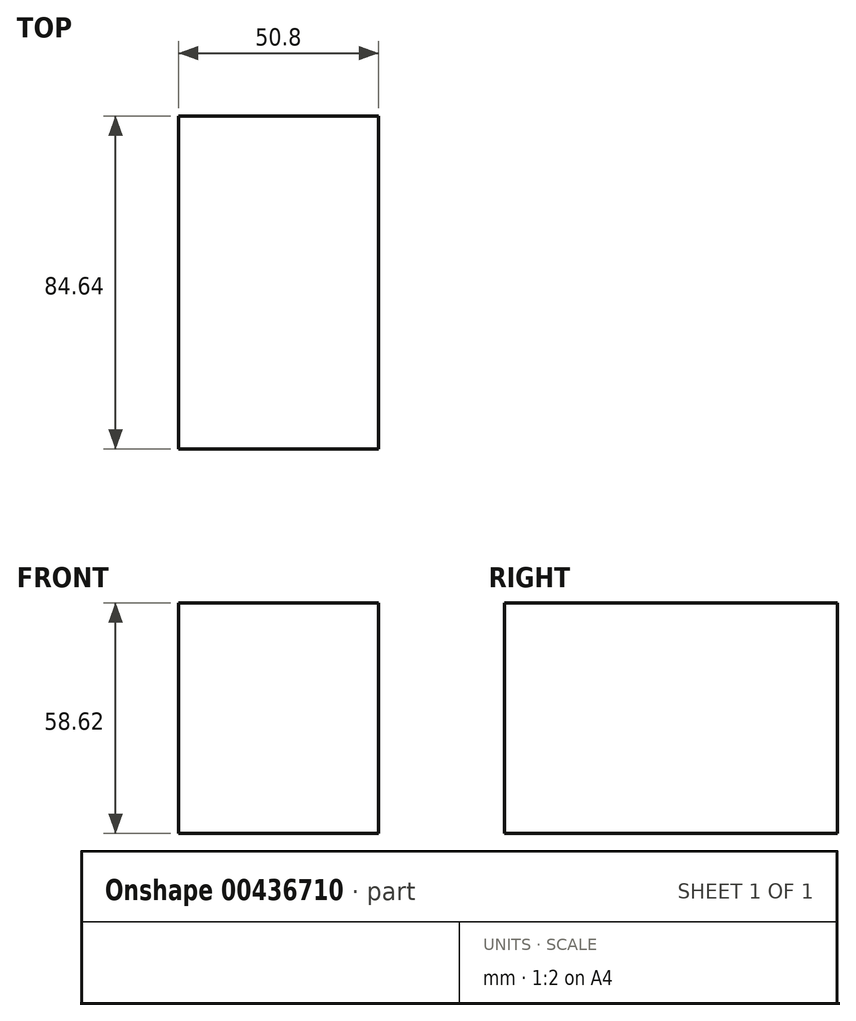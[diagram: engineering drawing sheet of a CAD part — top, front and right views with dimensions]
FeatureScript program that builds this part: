
annotation { "Feature Type Name" : "Feature", "Feature Type Description" : "" }
export const myFeature = defineFeature(function(context is Context, id is Id, definition is map)
    precondition{}
    {
        {
            var Q0;
            Q0=qCreatedBy(makeId("Right.planeOp"),FACE);
            var sketch = newSketch(context, id + "F0", { "sketchPlane" : qUnion([Q0])});
            skLineSegment(sketch, "E0.bottom", {"start": v(42.32, -29.3) * mm, "end": v(-42.32, -29.3) * mm});
            skLineSegment(sketch, "E0.top", {"start": v(42.32, 29.3) * mm, "end": v(-42.32, 29.3) * mm});
            skLineSegment(sketch, "E0.left", {"start": v(42.32, -29.3) * mm, "end": v(42.32, 29.3) * mm});
            skLineSegment(sketch, "E0.right", {"start": v(-42.32, -29.3) * mm, "end": v(-42.32, 29.3) * mm});
            skPoint(sketch, "E0.middle", {"position": v(0, 0) * mm});
            skSolve(sketch);
        }
        {
            var Q0;
            Q0 = qSketchRegion(id + "F0", true);
            extrude(context, id + "F1", {"entities" : qUnion([Q0]), "endBound" : BoundingType.SYMMETRIC, "depth" : 50.8 * mm});
        }
    });
